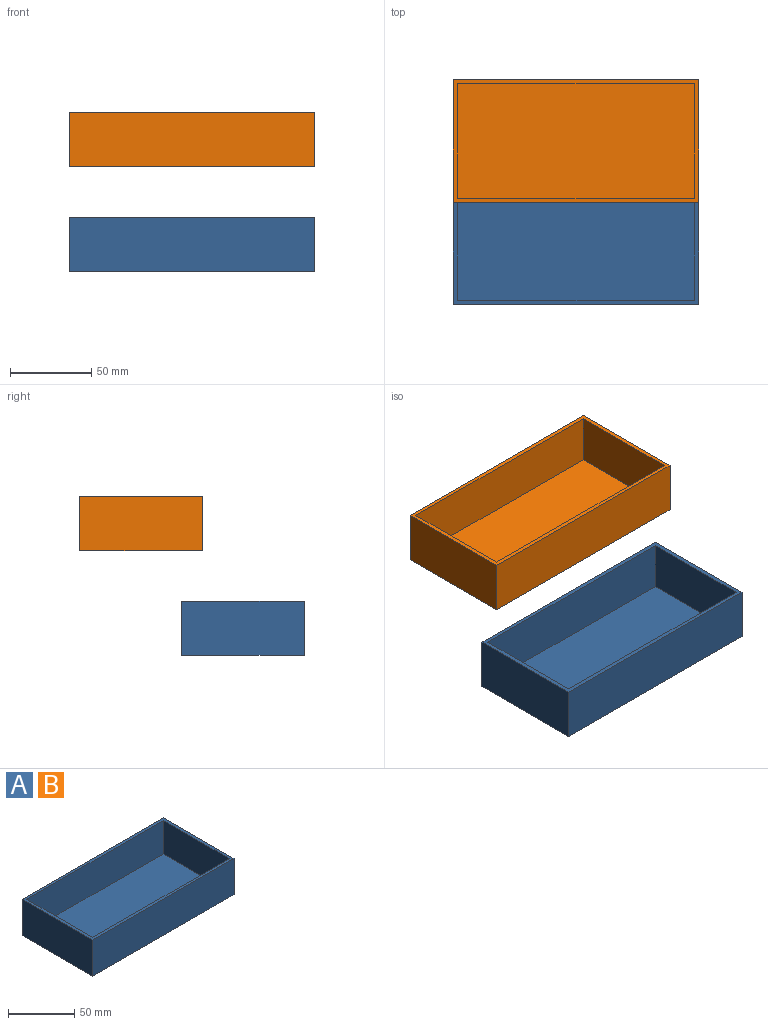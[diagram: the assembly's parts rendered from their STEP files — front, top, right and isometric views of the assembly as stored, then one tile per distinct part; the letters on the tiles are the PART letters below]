
ASSEMBLY  parts=2 mates=2
PART A: 11 faces, bbox 150.7x75.4x33.3 mm
  f0: plane 150.66x75.44mm, normal (0,0,1), area 1122.8mm2, adj f1,f3,f4,f5,f6,f8,f9,f10
  f1: plane 75.44x33.33mm, normal (-1,0,0), area 2514.7mm2, adj f0,f2,f4,f5
  f2: plane 150.66x75.44mm, normal (0,0,-1), area 11365.8mm2, adj f1,f3,f4,f5
  f3: plane 75.44x33.33mm, normal (1,0,0), area 2514.7mm2, adj f0,f2,f4,f5
  f4: plane 150.66x33.33mm, normal (0,-1,0), area 5022.3mm2, adj f0,f1,f2,f3
  f5: plane 150.66x33.33mm, normal (0,1,0), area 5022.3mm2, adj f0,f1,f2,f3
  f6: plane 70.36x30.79mm, normal (1,0,0), area 2166.6mm2, adj f0,f7,f9,f10
  f7: plane 145.58x70.36mm, normal (0,0,1), area 10243mm2, adj f6,f8,f9,f10
  f8: plane 70.36x30.79mm, normal (-1,0,0), area 2166.6mm2, adj f0,f7,f9,f10
  f9: plane 145.58x30.79mm, normal (0,1,0), area 4483.2mm2, adj f0,f6,f7,f8
  f10: plane 145.58x30.79mm, normal (0,-1,0), area 4483.2mm2, adj f0,f6,f7,f8
PART B: same geometry as A
PLACE A t=(-156.99,-34.74,23.73)mm
PLACE B t=(-156.99,27.87,87.91)mm
MATE planar B.f1 <-> A.f1  axis (-1,0,0) through (-232.32,-9.85,104.58)mm
MATE planar B.f3 <-> B.f3  axis (1,0,0) through (-81.66,-9.85,104.58)mm
